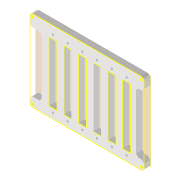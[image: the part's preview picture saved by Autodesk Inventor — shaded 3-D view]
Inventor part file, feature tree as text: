
AUTODESK INVENTOR PART (.ipt)
format: ipt  version: 2022 (Build 260153000, 153)  size: 580,096 bytes
history: native  units: mm
features: sketch x4, reference x4, other x4, extrude x3, projected_geometry x2, plane x1, pattern_linear x1, fillet x1, chamfer x1
ambient origin geometry x8: Origin, YZ Plane, XZ Plane, XY Plane, X Axis, Y Axis, Z Axis, Center Point
bodies: Volumenkörper1 (feature_tree)
feature tree (21):
  plane  "Arbeitsebene1"
  extrude  "Extrusion1"  Depth=3.5mm
  extrude  "Extrusion2"  Depth=2.8mm
  pattern_linear  "Rechteckige Anordnung1"  Spacing1=8.0mm  [1 undecoded]
  fillet  "Rundung1"  Radius=1.0mm
  sketch  "Skizze3"  dims[d4=2.8mm]
  extrude  "Extrusion3"  Depth=15.0mm
  chamfer  "Fase1"  Distance=0.5mm
  sketch  "Skizze1"  dims[d0=6.0mm d1=3.5mm]
  reference  "Referenz1"
  sketch  "Skizze2"  dims[d2=2.8mm d3=2.8mm]
  reference  "Referenz2"
  reference  "Referenz3"
  reference  "Referenz4"
  projected_geometry  "Projizierte Kontur1"
  sketch  "Skizze4"  dims[d5=3.0mm d6=8.0mm d7=0.0mm d8=1.0mm d9=1.0mm d11=0.5mm d12=8.4mm d13=0.0mm d14=0.0mm d15=60.0mm d17=18.7mm d18=4.0mm d19=2.8mm d20=2.8mm d21=5.0mm d22=5.0mm d23=10.0mm d24=15.0mm d25=0.0mm d26=0.0mm d27=3.0mm d28=2.0mm d29=45.0deg]
  projected_geometry  "Projizierte Kontur2"
  other  "Baugruppe1"
  other  "00_Omniscope_PCB_USBC:1"
  other  "00_Seeeduino Xiao:19"
  other  "00_Seeeduino Xiao:1"
note: 1 required parameter value undecoded (feature->parameter linkage not recoverable at this tier; creation-order binding heuristic only, values carry confidence <= 0.55)
